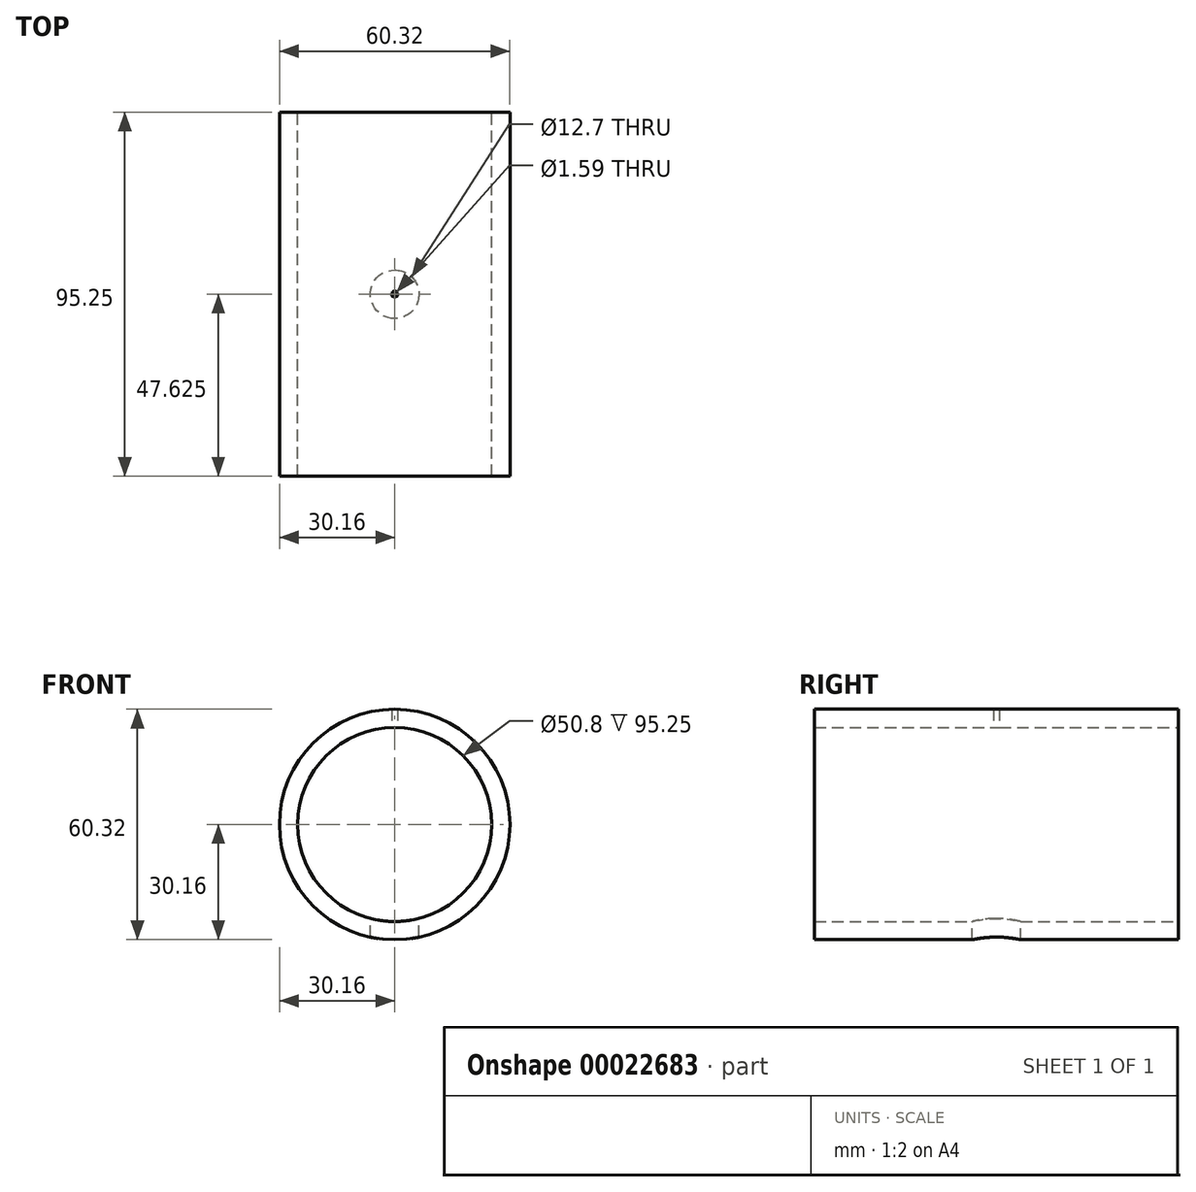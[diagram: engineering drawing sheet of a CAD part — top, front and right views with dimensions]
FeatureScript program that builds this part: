
annotation { "Feature Type Name" : "Feature", "Feature Type Description" : "" }
export const myFeature = defineFeature(function(context is Context, id is Id, definition is map)
    precondition{}
    {
        {
            var Q0;
            Q0=qCreatedBy(makeId("Front.planeOp"),FACE);
            var sketch = newSketch(context, id + "F0", { "sketchPlane" : qUnion([Q0])});
            skCircle(sketch, "E0", {"center": v(0, 0) * mm, "radius": 25.4 * mm});
            skCircle(sketch, "E1", {"center": v(0, 0) * mm, "radius": 30.16 * mm});
            skLineSegment(sketch, "E2", {"start": v(0, 30.16) * mm, "end": v(0, 10.05) * mm});
            skSolve(sketch);
        }
        {
            var Q0;
            Q0=qSketchRegion(id+"F0",true);
            extrude(context, id + "F1", {"entities" : qUnion([Q0]), "depth" : 95.25 * mm});
        }
        {
            var Q0;
            Q0=qCreatedBy(makeId("Top.planeOp"),FACE);
            var sketch = newSketch(context, id + "F2", { "sketchPlane" : qUnion([Q0])});
            skPoint(sketch, "E3", {"position": v(0, -47.63) * mm});
            skSolve(sketch);
        }
        {
            var Q0;
            Q0=sQuery(id+"F2.wireOp",VERTEX,"E3");
            var Q1;
            Q1=makeQuery(id+"F1.opExtrude","SWEPT_BODY",BODY,{"disambiguationData":[OSD([sQuery(id+"F0.wireOp",EDGE,"E0"),sQuery(id+"F0.wireOp",EDGE,"E1")])]});
            hole(context, id + "F3", {"style" : HoleStyle.SIMPLE, "holeDiameter" : 12.7 * mm, "endStyle" : HoleEndStyle.THROUGH, "locations" : qUnion([Q0]), "scope" : qUnion([Q1])});
        }
        {
            var Q0;
            Q0=qCreatedBy(makeId("Top.planeOp"),FACE);
            var sketch = newSketch(context, id + "F4", { "sketchPlane" : qUnion([Q0])});
            skPoint(sketch, "E4", {"position": v(0, -47.63) * mm});
            skSolve(sketch);
        }
        {
            var Q0;
            Q0=sQuery(id+"F4.wireOp",VERTEX,"E4");
            var Q1;
            Q1=makeQuery(id+"F1.opExtrude","SWEPT_BODY",BODY,{"disambiguationData":[OSD([sQuery(id+"F0.wireOp",EDGE,"E0"),sQuery(id+"F0.wireOp",EDGE,"E1")])]});
            hole(context, id + "F5", {"style" : HoleStyle.SIMPLE, "holeDiameter" : 1.59 * mm, "endStyle" : HoleEndStyle.THROUGH, "oppositeDirection" : true, "locations" : qUnion([Q0]), "scope" : qUnion([Q1])});
        }
    });
